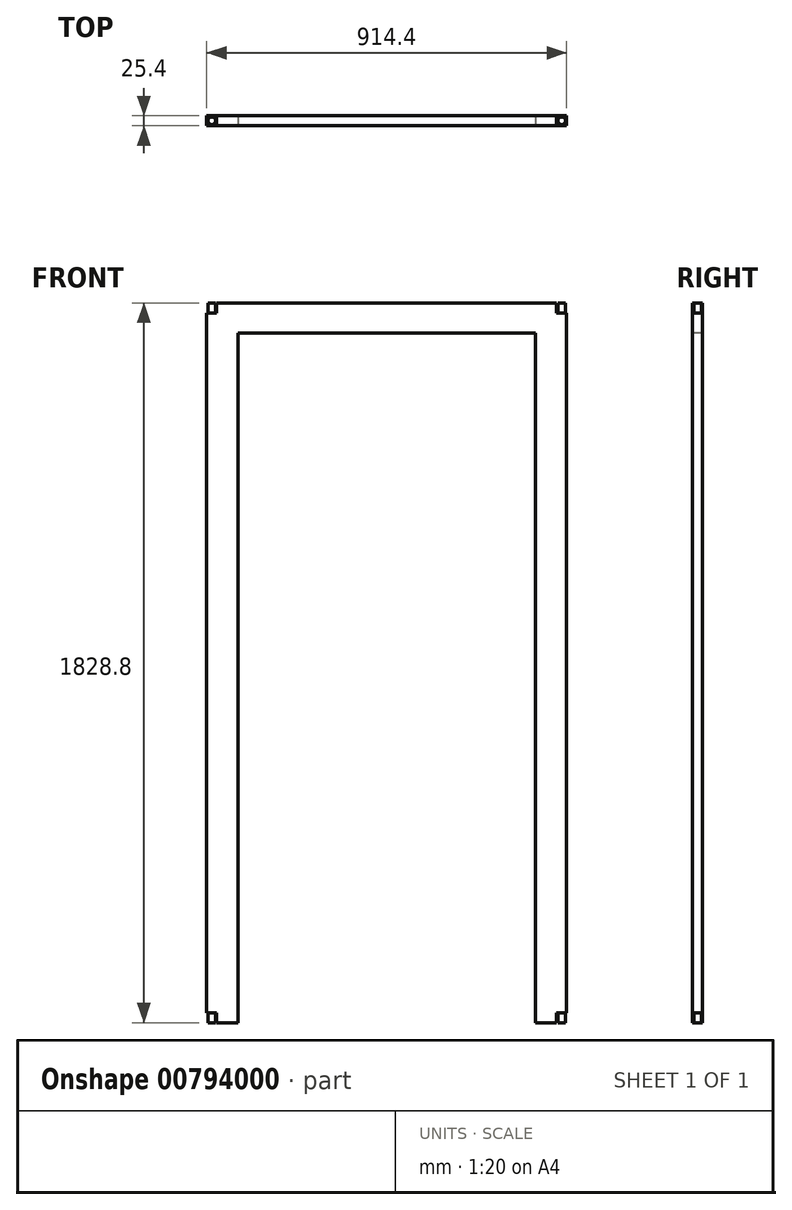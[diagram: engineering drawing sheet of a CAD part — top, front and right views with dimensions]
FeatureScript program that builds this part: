
annotation { "Feature Type Name" : "Feature", "Feature Type Description" : "" }
export const myFeature = defineFeature(function(context is Context, id is Id, definition is map)
    precondition{}
    {
        {
            var Q0;
            Q0=qCreatedBy(makeId("Front.planeOp"),FACE);
            var sketch = newSketch(context, id + "F0", { "sketchPlane" : qUnion([Q0])});
            skLineSegment(sketch, "E0.bottom", {"start": v(457.2, -914.4) * mm, "end": v(-457.2, -914.4) * mm});
            skLineSegment(sketch, "E0.top", {"start": v(457.2, 914.4) * mm, "end": v(-457.2, 914.4) * mm});
            skLineSegment(sketch, "E0.left", {"start": v(457.2, -914.4) * mm, "end": v(457.2, 914.4) * mm});
            skLineSegment(sketch, "E0.right", {"start": v(-457.2, -914.4) * mm, "end": v(-457.2, 914.4) * mm});
            skPoint(sketch, "E0.middle", {"position": v(0, 0) * mm});
            skSolve(sketch);
        }
        {
            var Q0;
            Q0=qSketchRegion(id+"F0",true);
            extrude(context, id + "F1", {"entities" : qUnion([Q0]), "depth" : 25.4 * mm, "offsetDistance" : 25.4 * mm});
        }
        {
            var Q0;
            Q0=makeQuery(id+"F1.opExtrude","SWEPT_FACE",FACE,{"disambiguationData":[OSD([sQuery(id+"F0.wireOp",EDGE,"E0.top")])]});
            var sketch = newSketch(context, id + "F2", { "sketchPlane" : qUnion([Q0])});
            skLineSegment(sketch, "E1.bottom", {"start": v(-457.2, 0) * mm, "end": v(-431.8, 0) * mm});
            skLineSegment(sketch, "E1.top", {"start": v(-457.2, -25.4) * mm, "end": v(-431.8, -25.4) * mm});
            skLineSegment(sketch, "E1.left", {"start": v(-457.2, 0) * mm, "end": v(-457.2, -25.4) * mm});
            skLineSegment(sketch, "E1.right", {"start": v(-431.8, 0) * mm, "end": v(-431.8, -25.4) * mm});
            skLineSegment(sketch, "E2.bottom", {"start": v(457.2, 0) * mm, "end": v(431.8, 0) * mm});
            skLineSegment(sketch, "E2.top", {"start": v(457.2, -25.4) * mm, "end": v(431.8, -25.4) * mm});
            skLineSegment(sketch, "E2.left", {"start": v(457.2, 0) * mm, "end": v(457.2, -25.4) * mm});
            skLineSegment(sketch, "E2.right", {"start": v(431.8, 0) * mm, "end": v(431.8, -25.4) * mm});
            skLineSegment(sketch, "E3.left", {"start": v(-457.2, -25.4) * mm, "end": v(-457.2, 0) * mm});
            skLineSegment(sketch, "E3.right", {"start": v(-431.8, -25.4) * mm, "end": v(-431.8, 0) * mm});
            skSolve(sketch);
        }
        {
            var Q0;
            Q0=qSketchRegion(id+"F2",true);
            extrude(context, id + "F3", {"entities" : qUnion([Q0]), "operationType" : NewBodyOperationType.REMOVE, "oppositeDirection" : true, "depth" : 25.4 * mm, "offsetDistance" : 25.4 * mm});
        }
        {
            var Q0;
            Q0=makeQuery(id+"F1.opExtrude","SWEPT_FACE",FACE,{"disambiguationData":[OSD([sQuery(id+"F0.wireOp",EDGE,"E0.bottom")])]});
            var sketch = newSketch(context, id + "F4", { "sketchPlane" : qUnion([Q0])});
            skLineSegment(sketch, "E4.bottom", {"start": v(-457.2, 25.4) * mm, "end": v(-431.8, 25.4) * mm});
            skLineSegment(sketch, "E4.top", {"start": v(-457.2, 0) * mm, "end": v(-431.8, 0) * mm});
            skLineSegment(sketch, "E4.left", {"start": v(-457.2, 25.4) * mm, "end": v(-457.2, 0) * mm});
            skLineSegment(sketch, "E4.right", {"start": v(-431.8, 25.4) * mm, "end": v(-431.8, 0) * mm});
            skLineSegment(sketch, "E5.bottom", {"start": v(457.2, 25.4) * mm, "end": v(431.8, 25.4) * mm});
            skLineSegment(sketch, "E5.top", {"start": v(457.2, 0) * mm, "end": v(431.8, 0) * mm});
            skLineSegment(sketch, "E5.left", {"start": v(457.2, 25.4) * mm, "end": v(457.2, 0) * mm});
            skLineSegment(sketch, "E5.right", {"start": v(431.8, 25.4) * mm, "end": v(431.8, 0) * mm});
            skSolve(sketch);
        }
        {
            var Q0;
            Q0=qSketchRegion(id+"F4",true);
            extrude(context, id + "F5", {"entities" : qUnion([Q0]), "operationType" : NewBodyOperationType.REMOVE, "oppositeDirection" : true, "depth" : 25.4 * mm, "offsetDistance" : 25.4 * mm});
        }
        {
            var Q0;
            Q0=makeQuery(id+"F3.boolean.opBoolean","COPY",FACE,{"derivedFrom":makeQuery(id+"F3.opExtrude","CAP_FACE",FACE,{"disambiguationData":[OSD([sQuery(id+"F2.wireOp",EDGE,"E1.top"),sQuery(id+"F2.wireOp",EDGE,"E1.bottom"),sQuery(id+"F2.wireOp",EDGE,"E3.left"),sQuery(id+"F2.wireOp",EDGE,"E3.right")])],"isStart":false})});
            var sketch = newSketch(context, id + "F6", { "sketchPlane" : qUnion([Q0])});
            skPoint(sketch, "E6", {"position": v(-444.5, 0) * mm});
            skPoint(sketch, "E7", {"position": v(-457.2, -12.7) * mm});
            skCircle(sketch, "E8", {"center": v(-444.5, -12.7) * mm, "radius": 9.53 * mm});
            skSolve(sketch);
        }
        {
            var Q0;
            Q0=qSketchRegion(id+"F6",true);
            extrude(context, id + "F7", {"entities" : qUnion([Q0]), "operationType" : NewBodyOperationType.ADD, "depth" : 25.4 * mm, "offsetDistance" : 25.4 * mm});
        }
        {
            var Q0;
            Q0=makeQuery(id+"F3.boolean.opBoolean","COPY",FACE,{"derivedFrom":makeQuery(id+"F3.opExtrude","CAP_FACE",FACE,{"disambiguationData":[OSD([sQuery(id+"F2.wireOp",EDGE,"E2.bottom"),sQuery(id+"F2.wireOp",EDGE,"E2.top"),sQuery(id+"F2.wireOp",EDGE,"E2.left"),sQuery(id+"F2.wireOp",EDGE,"E2.right")])],"isStart":false})});
            var sketch = newSketch(context, id + "F8", { "sketchPlane" : qUnion([Q0])});
            skPoint(sketch, "E9", {"position": v(444.5, 0) * mm});
            skPoint(sketch, "E10", {"position": v(457.2, -12.7) * mm});
            skCircle(sketch, "E11", {"center": v(444.5, -12.7) * mm, "radius": 9.53 * mm});
            skSolve(sketch);
        }
        {
            var Q0;
            Q0=qSketchRegion(id+"F8",true);
            extrude(context, id + "F9", {"entities" : qUnion([Q0]), "operationType" : NewBodyOperationType.ADD, "depth" : 25.4 * mm, "offsetDistance" : 25.4 * mm});
        }
        {
            var Q0;
            Q0=makeQuery(id+"F5.boolean.opBoolean","COPY",FACE,{"derivedFrom":makeQuery(id+"F5.opExtrude","CAP_FACE",FACE,{"disambiguationData":[OSD([sQuery(id+"F4.wireOp",EDGE,"E4.bottom"),sQuery(id+"F4.wireOp",EDGE,"E4.top"),sQuery(id+"F4.wireOp",EDGE,"E4.left"),sQuery(id+"F4.wireOp",EDGE,"E4.right")])],"isStart":false})});
            var sketch = newSketch(context, id + "F10", { "sketchPlane" : qUnion([Q0])});
            skPoint(sketch, "E12", {"position": v(-444.5, 25.4) * mm});
            skPoint(sketch, "E13", {"position": v(-457.2, 12.7) * mm});
            skCircle(sketch, "E14", {"center": v(-444.5, 12.7) * mm, "radius": 9.53 * mm});
            skSolve(sketch);
        }
        {
            var Q0;
            Q0=qSketchRegion(id+"F10",true);
            extrude(context, id + "F11", {"entities" : qUnion([Q0]), "operationType" : NewBodyOperationType.ADD, "depth" : 25.4 * mm, "offsetDistance" : 25.4 * mm});
        }
        {
            var Q0;
            Q0=makeQuery(id+"F5.boolean.opBoolean","COPY",FACE,{"derivedFrom":makeQuery(id+"F5.opExtrude","CAP_FACE",FACE,{"disambiguationData":[OSD([sQuery(id+"F4.wireOp",EDGE,"E5.bottom"),sQuery(id+"F4.wireOp",EDGE,"E5.top"),sQuery(id+"F4.wireOp",EDGE,"E5.left"),sQuery(id+"F4.wireOp",EDGE,"E5.right")])],"isStart":false})});
            var sketch = newSketch(context, id + "F12", { "sketchPlane" : qUnion([Q0])});
            skPoint(sketch, "E15", {"position": v(444.5, 25.4) * mm});
            skPoint(sketch, "E16", {"position": v(457.2, 12.7) * mm});
            skCircle(sketch, "E17", {"center": v(444.5, 12.7) * mm, "radius": 9.53 * mm});
            skSolve(sketch);
        }
        {
            var Q0;
            Q0=qSketchRegion(id+"F12",true);
            extrude(context, id + "F13", {"entities" : qUnion([Q0]), "operationType" : NewBodyOperationType.ADD, "depth" : 25.4 * mm, "offsetDistance" : 25.4 * mm});
        }
        {
            var Q0;
            Q0=makeQuery(id+"F1.opExtrude","CAP_FACE",FACE,{"disambiguationData":[OSD([sQuery(id+"F0.wireOp",EDGE,"E0.bottom"),sQuery(id+"F0.wireOp",EDGE,"E0.top"),sQuery(id+"F0.wireOp",EDGE,"E0.left"),sQuery(id+"F0.wireOp",EDGE,"E0.right")])],"isStart":false});
            var sketch = newSketch(context, id + "F14", { "sketchPlane" : qUnion([Q0])});
            skLineSegment(sketch, "E18", {"start": v(-431.8, -914.4) * mm, "end": v(431.8, -914.4) * mm});
            skLineSegment(sketch, "E19", {"start": v(431.8, -914.4) * mm, "end": v(0, -914.4) * mm});
            skLineSegment(sketch, "E20", {"start": v(0, -914.4) * mm, "end": v(215.9, -914.4) * mm});
            skLineSegment(sketch, "E21", {"start": v(215.9, -914.4) * mm, "end": v(431.8, -914.4) * mm});
            skLineSegment(sketch, "E22", {"start": v(431.8, -914.4) * mm, "end": v(323.85, -914.4) * mm});
            skLineSegment(sketch, "E23", {"start": v(0, -914.4) * mm, "end": v(-431.8, -914.4) * mm});
            skLineSegment(sketch, "E24", {"start": v(-431.8, -914.4) * mm, "end": v(-215.9, -914.4) * mm});
            skLineSegment(sketch, "E25", {"start": v(-215.9, -914.4) * mm, "end": v(-323.85, -914.4) * mm});
            skLineSegment(sketch, "E26", {"start": v(-323.85, -914.4) * mm, "end": v(-431.8, -914.4) * mm});
            skLineSegment(sketch, "E27", {"start": v(431.8, -914.4) * mm, "end": v(377.82, -914.4) * mm});
            skLineSegment(sketch, "E28.bottom", {"start": v(-377.83, -914.4) * mm, "end": v(377.82, -914.4) * mm});
            skLineSegment(sketch, "E28.top", {"start": v(-377.83, 838.2) * mm, "end": v(377.83, 838.2) * mm});
            skLineSegment(sketch, "E28.left", {"start": v(-377.83, -914.4) * mm, "end": v(-377.83, 838.2) * mm});
            skLineSegment(sketch, "E28.right", {"start": v(377.82, -914.4) * mm, "end": v(377.82, 838.2) * mm});
            skSolve(sketch);
        }
        {
            var Q0;
            Q0 = qSketchRegion(id + "F14", true);
            extrude(context, id + "F15", {"entities" : qUnion([Q0]), "operationType" : NewBodyOperationType.REMOVE, "oppositeDirection" : true, "depth" : 25.4 * mm, "offsetDistance" : 25.4 * mm});
        }
    });
